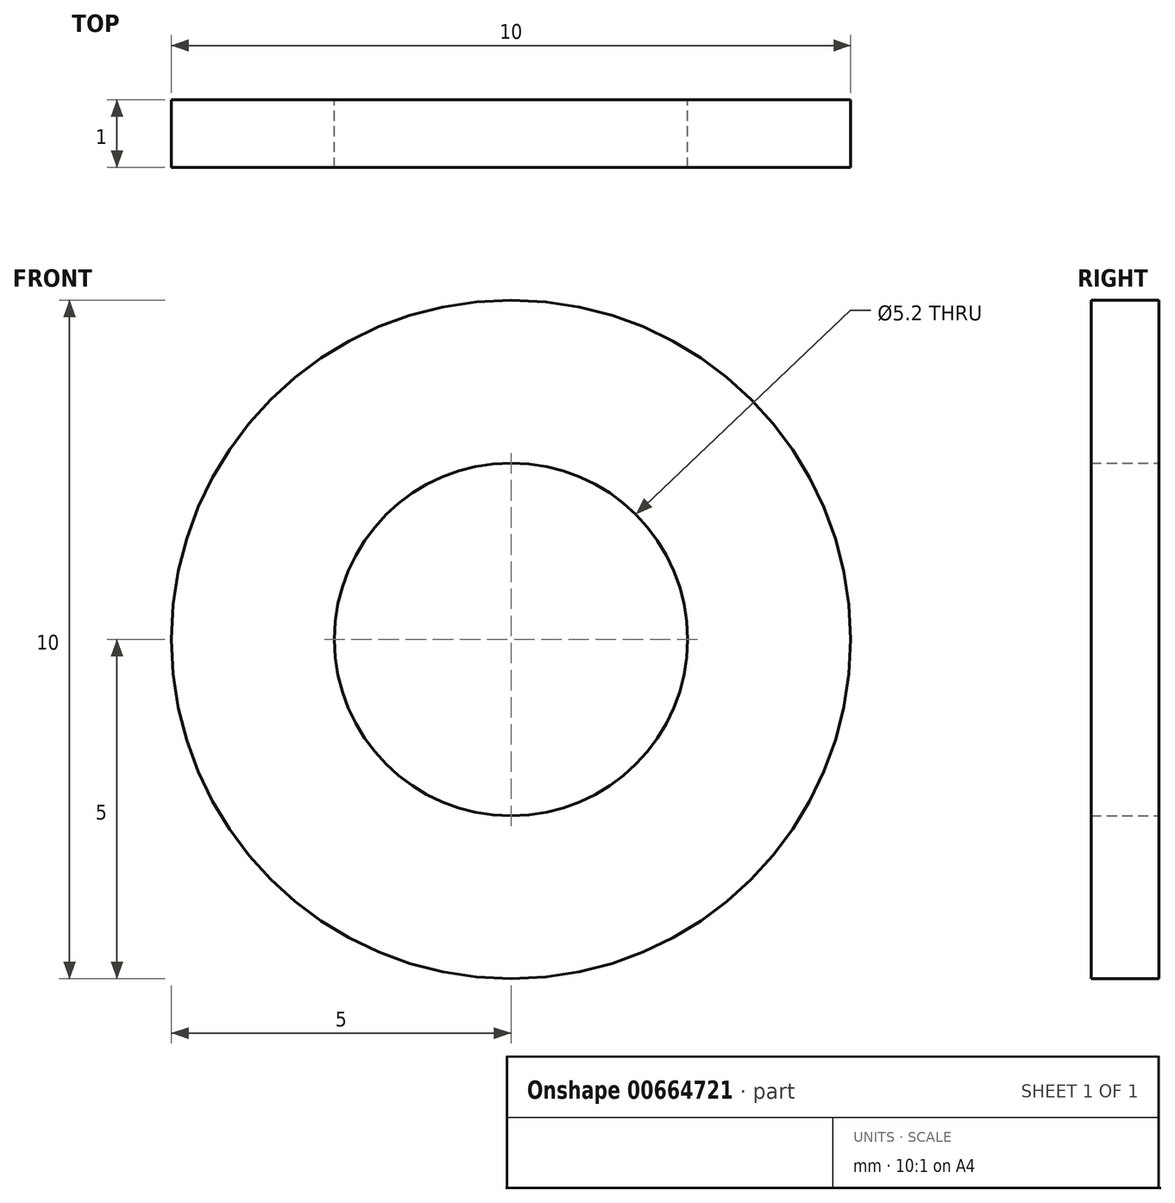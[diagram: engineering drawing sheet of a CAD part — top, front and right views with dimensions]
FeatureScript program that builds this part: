
annotation { "Feature Type Name" : "Feature", "Feature Type Description" : "" }
export const myFeature = defineFeature(function(context is Context, id is Id, definition is map)
    precondition{}
    {
        {
            var Q0;
            Q0=qCreatedBy(makeId("Front.planeOp"),FACE);
            var sketch = newSketch(context, id + "F0", { "sketchPlane" : qUnion([Q0])});
            skCircle(sketch, "E0", {"center": v(0, 0) * mm, "radius": 2.6 * mm});
            skCircle(sketch, "E1", {"center": v(0, 0) * mm, "radius": 5 * mm});
            skSolve(sketch);
        }
        {
            var Q0;
            Q0=makeQuery(id+"F0.imprint","IMPRINT",FACE,{"disambiguationData":[TD([[makeQuery(id+"F0.imprint","IMPRINT",EDGE,{"derivedFrom":sQuery(id+"F0.wireOp",EDGE,"E0")}),-1.0]])]});
            extrude(context, id + "F1", {"entities" : qUnion([Q0]), "depth" : 1 * mm, "offsetDistance" : 25 * mm});
        }
    });
